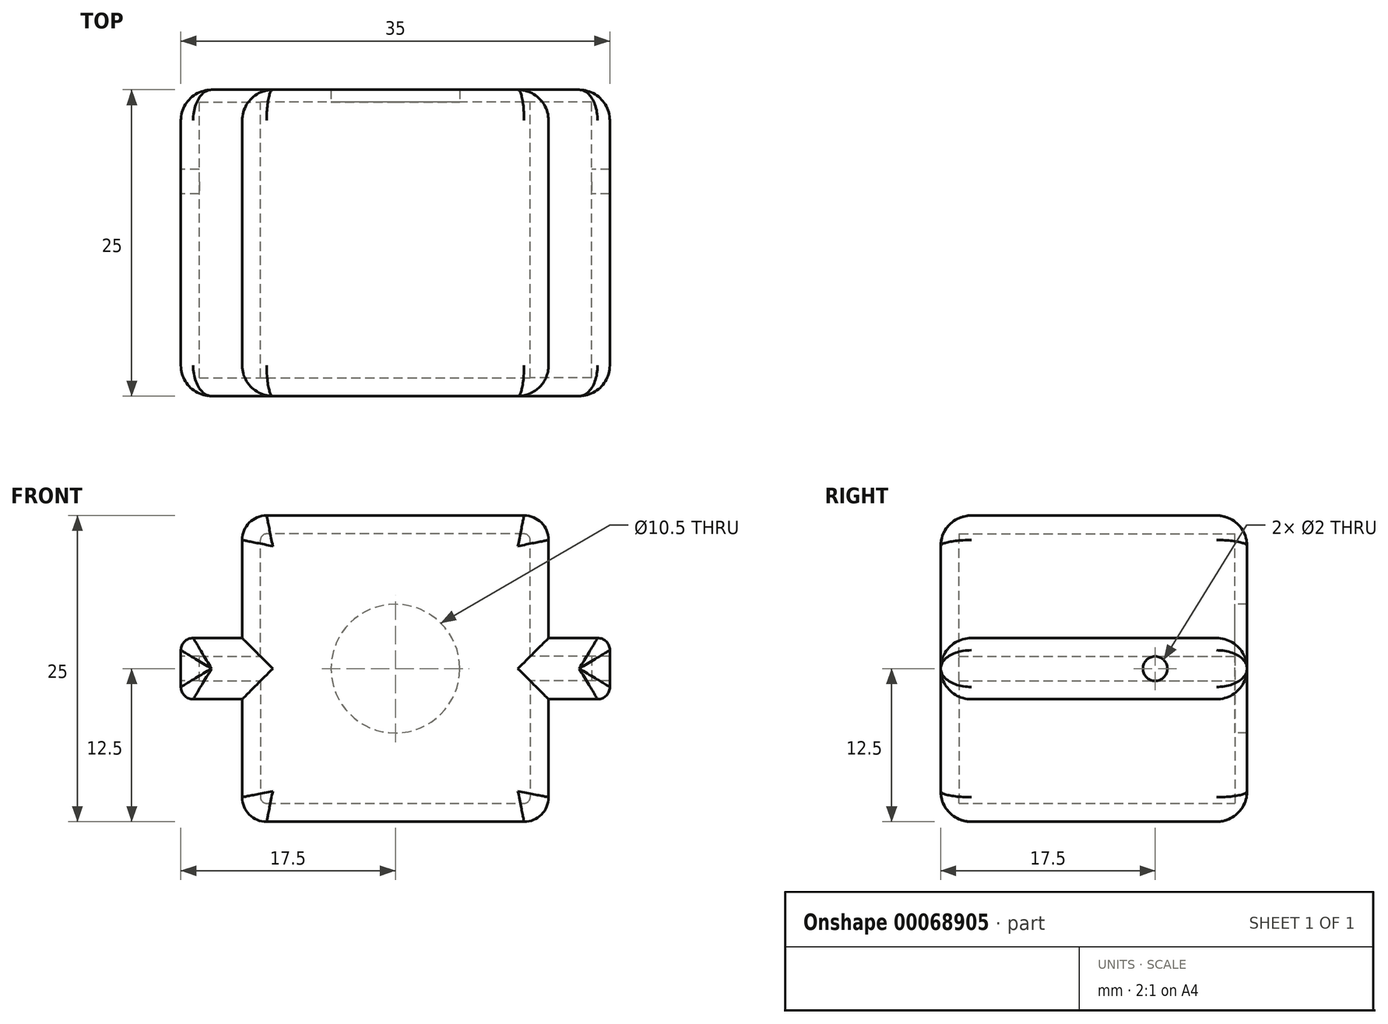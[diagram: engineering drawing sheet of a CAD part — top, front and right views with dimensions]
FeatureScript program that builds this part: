
annotation { "Feature Type Name" : "Feature", "Feature Type Description" : "" }
export const myFeature = defineFeature(function(context is Context, id is Id, definition is map)
    precondition{}
    {
        {
            var Q0;
            Q0=qCreatedBy(makeId("Front.planeOp"),FACE);
            var sketch = newSketch(context, id + "F0", { "sketchPlane" : qUnion([Q0])});
            skLineSegment(sketch, "E0", {"start": v(12.5, -2.5) * mm, "end": v(12.5, -10.5) * mm});
            skLineSegment(sketch, "E1", {"start": v(12.5, 2.5) * mm, "end": v(12.5, 10.5) * mm});
            skLineSegment(sketch, "E2", {"start": v(10.5, 12.5) * mm, "end": v(0, 12.5) * mm});
            skLineSegment(sketch, "E3", {"start": v(10.5, -12.5) * mm, "end": v(0, -12.5) * mm});
            skPoint(sketch, "E4.visualSharp", {"position": v(12.5, 12.5) * mm});
            skArc(sketch, "E4.filletArc", {"start": v(12.5, 10.5) * mm, "mid": v(11.91, 11.91) * mm, "end": v(10.5, 12.5) * mm});
            skPoint(sketch, "E5.visualSharp", {"position": v(12.5, -12.5) * mm});
            skArc(sketch, "E5.filletArc", {"start": v(10.5, -12.5) * mm, "mid": v(11.91, -11.91) * mm, "end": v(12.5, -10.5) * mm});
            skArc(sketch, "E6.MirrorCS", {"start": v(-12.5, 10.5) * mm, "mid": v(-11.91, 11.91) * mm, "end": v(-10.5, 12.5) * mm});
            skArc(sketch, "E7.MirrorCS", {"start": v(-10.5, -12.5) * mm, "mid": v(-11.91, -11.91) * mm, "end": v(-12.5, -10.5) * mm});
            skLineSegment(sketch, "E8.MirrorCS", {"start": v(-12.5, 2.5) * mm, "end": v(-12.5, 10.5) * mm});
            skLineSegment(sketch, "E9.MirrorCS", {"start": v(-10.5, 12.5) * mm, "end": v(0, 12.5) * mm});
            skLineSegment(sketch, "E10.MirrorCS", {"start": v(-12.5, -2.5) * mm, "end": v(-12.5, -10.5) * mm});
            skLineSegment(sketch, "E11.MirrorCS", {"start": v(-10.5, -12.5) * mm, "end": v(0, -12.5) * mm});
            skPoint(sketch, "E12.MirrorP", {"position": v(-12.5, -12.5) * mm});
            skPoint(sketch, "E13.MirrorP", {"position": v(-12.5, 12.5) * mm});
            skCircle(sketch, "E14", {"center": v(0, 0) * mm, "radius": 5.25 * mm});
            skLineSegment(sketch, "E15", {"start": v(17.5, 0) * mm, "end": v(17.5, 1.5) * mm});
            skLineSegment(sketch, "E16", {"start": v(16.5, 2.5) * mm, "end": v(12.5, 2.5) * mm});
            skPoint(sketch, "E17.visualSharp", {"position": v(17.5, 2.5) * mm});
            skArc(sketch, "E17.filletArc", {"start": v(17.5, 1.5) * mm, "mid": v(17.2, 2.2) * mm, "end": v(16.5, 2.5) * mm});
            skArc(sketch, "E18.MirrorCS", {"start": v(17.5, -1.5) * mm, "mid": v(17.2, -2.2) * mm, "end": v(16.5, -2.5) * mm});
            skLineSegment(sketch, "E19.MirrorCS", {"start": v(16.5, -2.5) * mm, "end": v(12.5, -2.5) * mm});
            skLineSegment(sketch, "E20.MirrorCS", {"start": v(17.5, 0) * mm, "end": v(17.5, -1.5) * mm});
            skPoint(sketch, "E21.MirrorP", {"position": v(17.5, -2.5) * mm});
            skArc(sketch, "E22.MirrorCS", {"start": v(-17.5, 1.5) * mm, "mid": v(-17.2, 2.2) * mm, "end": v(-16.5, 2.5) * mm});
            skLineSegment(sketch, "E23.MirrorCS", {"start": v(-17.5, 0) * mm, "end": v(-17.5, 1.5) * mm});
            skArc(sketch, "E24.MirrorCS", {"start": v(-17.5, -1.5) * mm, "mid": v(-17.2, -2.2) * mm, "end": v(-16.5, -2.5) * mm});
            skLineSegment(sketch, "E25.MirrorCS", {"start": v(-17.5, 0) * mm, "end": v(-17.5, -1.5) * mm});
            skPoint(sketch, "E26.MirrorP", {"position": v(-17.5, -2.5) * mm});
            skLineSegment(sketch, "E27.MirrorCS", {"start": v(-16.5, -2.5) * mm, "end": v(-12.5, -2.5) * mm});
            skLineSegment(sketch, "E28.MirrorCS", {"start": v(-16.5, 2.5) * mm, "end": v(-12.5, 2.5) * mm});
            skPoint(sketch, "E29.MirrorP", {"position": v(-17.5, 2.5) * mm});
            skPoint(sketch, "E30.orphan", {"position": v(-12.5, 0) * mm});
            skPoint(sketch, "E31.orphan", {"position": v(12.5, 0) * mm});
            skSolve(sketch);
        }
        {
            var Q0;
            Q0=qSketchRegion(id+"F0",true);
            extrude(context, id + "F1", {"entities" : qUnion([Q0]), "oppositeDirection" : true, "depth" : 1 * mm});
        }
        {
            var Q0;
            Q0=qCreatedBy(makeId("Front.planeOp"),FACE);
            var sketch = newSketch(context, id + "F2", { "sketchPlane" : qUnion([Q0])});
            skLineSegment(sketch, "E32", {"start": v(12.5, -2.5) * mm, "end": v(12.5, -10.5) * mm});
            skLineSegment(sketch, "E33", {"start": v(12.5, 2.5) * mm, "end": v(12.5, 10.5) * mm});
            skLineSegment(sketch, "E34", {"start": v(10.5, 12.5) * mm, "end": v(0, 12.5) * mm});
            skLineSegment(sketch, "E35", {"start": v(10.5, -12.5) * mm, "end": v(0, -12.5) * mm});
            skPoint(sketch, "E36.visualSharp", {"position": v(12.5, 12.5) * mm});
            skArc(sketch, "E36.filletArc", {"start": v(12.5, 10.5) * mm, "mid": v(11.91, 11.91) * mm, "end": v(10.5, 12.5) * mm});
            skPoint(sketch, "E37.visualSharp", {"position": v(12.5, -12.5) * mm});
            skArc(sketch, "E37.filletArc", {"start": v(10.5, -12.5) * mm, "mid": v(11.91, -11.91) * mm, "end": v(12.5, -10.5) * mm});
            skArc(sketch, "E38.MirrorCS", {"start": v(-12.5, 10.5) * mm, "mid": v(-11.91, 11.91) * mm, "end": v(-10.5, 12.5) * mm});
            skArc(sketch, "E39.MirrorCS", {"start": v(-10.5, -12.5) * mm, "mid": v(-11.91, -11.91) * mm, "end": v(-12.5, -10.5) * mm});
            skLineSegment(sketch, "E40.MirrorCS", {"start": v(-12.5, 2.5) * mm, "end": v(-12.5, 10.5) * mm});
            skLineSegment(sketch, "E41.MirrorCS", {"start": v(-10.5, 12.5) * mm, "end": v(0, 12.5) * mm});
            skLineSegment(sketch, "E42.MirrorCS", {"start": v(-12.5, -2.5) * mm, "end": v(-12.5, -10.5) * mm});
            skLineSegment(sketch, "E43.MirrorCS", {"start": v(-10.5, -12.5) * mm, "end": v(0, -12.5) * mm});
            skPoint(sketch, "E44.MirrorP", {"position": v(-12.87, -12.78) * mm});
            skPoint(sketch, "E45.MirrorP", {"position": v(-12.87, 12.22) * mm});
            skLineSegment(sketch, "E46", {"start": v(17.5, 0) * mm, "end": v(17.5, 1.5) * mm});
            skLineSegment(sketch, "E47", {"start": v(16.5, 2.5) * mm, "end": v(12.5, 2.5) * mm});
            skPoint(sketch, "E48.visualSharp", {"position": v(17.5, 2.5) * mm});
            skArc(sketch, "E48.filletArc", {"start": v(17.5, 1.5) * mm, "mid": v(17.2, 2.2) * mm, "end": v(16.5, 2.5) * mm});
            skArc(sketch, "E49.MirrorCS", {"start": v(17.5, -1.5) * mm, "mid": v(17.2, -2.2) * mm, "end": v(16.5, -2.5) * mm});
            skLineSegment(sketch, "E50.MirrorCS", {"start": v(16.5, -2.5) * mm, "end": v(12.5, -2.5) * mm});
            skLineSegment(sketch, "E51.MirrorCS", {"start": v(17.5, 0) * mm, "end": v(17.5, -1.5) * mm});
            skPoint(sketch, "E52.MirrorP", {"position": v(17.13, -2.78) * mm});
            skArc(sketch, "E53.MirrorCS", {"start": v(-17.5, 1.5) * mm, "mid": v(-17.2, 2.2) * mm, "end": v(-16.5, 2.5) * mm});
            skLineSegment(sketch, "E54.MirrorCS", {"start": v(-17.5, 0) * mm, "end": v(-17.5, 1.5) * mm});
            skArc(sketch, "E55.MirrorCS", {"start": v(-17.5, -1.5) * mm, "mid": v(-17.2, -2.2) * mm, "end": v(-16.5, -2.5) * mm});
            skLineSegment(sketch, "E56.MirrorCS", {"start": v(-17.5, 0) * mm, "end": v(-17.5, -1.5) * mm});
            skPoint(sketch, "E57.MirrorP", {"position": v(-17.87, -2.78) * mm});
            skLineSegment(sketch, "E58.MirrorCS", {"start": v(-16.5, -2.5) * mm, "end": v(-12.5, -2.5) * mm});
            skLineSegment(sketch, "E59.MirrorCS", {"start": v(-16.5, 2.5) * mm, "end": v(-12.5, 2.5) * mm});
            skPoint(sketch, "E60.MirrorP", {"position": v(-17.87, 2.22) * mm});
            skPoint(sketch, "E61.orphan", {"position": v(-12.5, 0) * mm});
            skPoint(sketch, "E62.orphan", {"position": v(12.5, 0) * mm});
            skSolve(sketch);
        }
        {
            var Q0;
            Q0=qSketchRegion(id+"F2",true);
            extrude(context, id + "F3", {"entities" : qUnion([Q0]), "depth" : 24 * mm});
        }
        {
            var Q0;
            Q0=makeQuery(id+"F3.opExtrude","CAP_FACE",FACE,{"disambiguationData":[OSD([sQuery(id+"F2.wireOp",EDGE,"E32"),sQuery(id+"F2.wireOp",EDGE,"E33"),sQuery(id+"F2.wireOp",EDGE,"E34"),sQuery(id+"F2.wireOp",EDGE,"E35"),sQuery(id+"F2.wireOp",EDGE,"E36.filletArc"),sQuery(id+"F2.wireOp",EDGE,"E37.filletArc"),sQuery(id+"F2.wireOp",EDGE,"E38.MirrorCS"),sQuery(id+"F2.wireOp",EDGE,"E39.MirrorCS"),sQuery(id+"F2.wireOp",EDGE,"E40.MirrorCS"),sQuery(id+"F2.wireOp",EDGE,"E41.MirrorCS"),sQuery(id+"F2.wireOp",EDGE,"E42.MirrorCS"),sQuery(id+"F2.wireOp",EDGE,"E43.MirrorCS"),sQuery(id+"F2.wireOp",EDGE,"E46"),sQuery(id+"F2.wireOp",EDGE,"E47"),sQuery(id+"F2.wireOp",EDGE,"E48.filletArc"),sQuery(id+"F2.wireOp",EDGE,"E49.MirrorCS"),sQuery(id+"F2.wireOp",EDGE,"E50.MirrorCS"),sQuery(id+"F2.wireOp",EDGE,"E51.MirrorCS"),sQuery(id+"F2.wireOp",EDGE,"E53.MirrorCS"),sQuery(id+"F2.wireOp",EDGE,"E54.MirrorCS"),sQuery(id+"F2.wireOp",EDGE,"E55.MirrorCS"),sQuery(id+"F2.wireOp",EDGE,"E56.MirrorCS"),sQuery(id+"F2.wireOp",EDGE,"E58.MirrorCS"),sQuery(id+"F2.wireOp",EDGE,"E59.MirrorCS")])],"isStart":true});
            shell(context, id + "F4", {"entities" : qUnion([Q0]), "thickness" : 1.5 * mm});
        }
        {
            var Q0;
            Q0=makeQuery(id+"F1.opExtrude","SWEPT_BODY",BODY,{"disambiguationData":[OSD([sQuery(id+"F0.wireOp",EDGE,"E0"),sQuery(id+"F0.wireOp",EDGE,"E1"),sQuery(id+"F0.wireOp",EDGE,"E2"),sQuery(id+"F0.wireOp",EDGE,"E3"),sQuery(id+"F0.wireOp",EDGE,"E4.filletArc"),sQuery(id+"F0.wireOp",EDGE,"E5.filletArc"),sQuery(id+"F0.wireOp",EDGE,"E6.MirrorCS"),sQuery(id+"F0.wireOp",EDGE,"E7.MirrorCS"),sQuery(id+"F0.wireOp",EDGE,"E8.MirrorCS"),sQuery(id+"F0.wireOp",EDGE,"E9.MirrorCS"),sQuery(id+"F0.wireOp",EDGE,"E10.MirrorCS"),sQuery(id+"F0.wireOp",EDGE,"E11.MirrorCS"),sQuery(id+"F0.wireOp",EDGE,"E14"),sQuery(id+"F0.wireOp",EDGE,"E15"),sQuery(id+"F0.wireOp",EDGE,"E16"),sQuery(id+"F0.wireOp",EDGE,"E17.filletArc"),sQuery(id+"F0.wireOp",EDGE,"E18.MirrorCS"),sQuery(id+"F0.wireOp",EDGE,"E19.MirrorCS"),sQuery(id+"F0.wireOp",EDGE,"E20.MirrorCS"),sQuery(id+"F0.wireOp",EDGE,"E22.MirrorCS"),sQuery(id+"F0.wireOp",EDGE,"E23.MirrorCS"),sQuery(id+"F0.wireOp",EDGE,"E24.MirrorCS"),sQuery(id+"F0.wireOp",EDGE,"E25.MirrorCS"),sQuery(id+"F0.wireOp",EDGE,"E27.MirrorCS"),sQuery(id+"F0.wireOp",EDGE,"E28.MirrorCS")])]});
            var Q1;
            Q1=makeQuery(id+"F3.opExtrude","SWEPT_BODY",BODY,{"disambiguationData":[OSD([sQuery(id+"F2.wireOp",EDGE,"E32"),sQuery(id+"F2.wireOp",EDGE,"E33"),sQuery(id+"F2.wireOp",EDGE,"E34"),sQuery(id+"F2.wireOp",EDGE,"E35"),sQuery(id+"F2.wireOp",EDGE,"E36.filletArc"),sQuery(id+"F2.wireOp",EDGE,"E37.filletArc"),sQuery(id+"F2.wireOp",EDGE,"E38.MirrorCS"),sQuery(id+"F2.wireOp",EDGE,"E39.MirrorCS"),sQuery(id+"F2.wireOp",EDGE,"E40.MirrorCS"),sQuery(id+"F2.wireOp",EDGE,"E41.MirrorCS"),sQuery(id+"F2.wireOp",EDGE,"E42.MirrorCS"),sQuery(id+"F2.wireOp",EDGE,"E43.MirrorCS"),sQuery(id+"F2.wireOp",EDGE,"E46"),sQuery(id+"F2.wireOp",EDGE,"E47"),sQuery(id+"F2.wireOp",EDGE,"E48.filletArc"),sQuery(id+"F2.wireOp",EDGE,"E49.MirrorCS"),sQuery(id+"F2.wireOp",EDGE,"E50.MirrorCS"),sQuery(id+"F2.wireOp",EDGE,"E51.MirrorCS"),sQuery(id+"F2.wireOp",EDGE,"E53.MirrorCS"),sQuery(id+"F2.wireOp",EDGE,"E54.MirrorCS"),sQuery(id+"F2.wireOp",EDGE,"E55.MirrorCS"),sQuery(id+"F2.wireOp",EDGE,"E56.MirrorCS"),sQuery(id+"F2.wireOp",EDGE,"E58.MirrorCS"),sQuery(id+"F2.wireOp",EDGE,"E59.MirrorCS")])]});
            booleanBodies(context, id + "F5", {"operationType" : BooleanOperationType.UNION, "tools" : qUnion([Q0, Q1])});
        }
        {
            var Q0;
            Q0=makeQuery(id+"F3.opExtrude","CAP_EDGE",EDGE,{"disambiguationData":[OSD([sQuery(id+"F2.wireOp",EDGE,"E34"),sQuery(id+"F2.wireOp",EDGE,"E41.MirrorCS")])],"isStart":false});
            var Q1;
            Q1=makeQuery(id+"F3.opExtrude","CAP_EDGE",EDGE,{"disambiguationData":[OSD([sQuery(id+"F2.wireOp",EDGE,"E35"),sQuery(id+"F2.wireOp",EDGE,"E43.MirrorCS")])],"isStart":false});
            var Q2;
            Q2=makeQuery(id+"F3.opExtrude","CAP_EDGE",EDGE,{"disambiguationData":[OSD([sQuery(id+"F2.wireOp",EDGE,"E59.MirrorCS")])],"isStart":false});
            var Q3;
            Q3=makeQuery(id+"F3.opExtrude","CAP_EDGE",EDGE,{"disambiguationData":[OSD([sQuery(id+"F2.wireOp",EDGE,"E47")])],"isStart":false});
            var Q4;
            Q4=makeQuery(id+"F1.opExtrude","CAP_EDGE",EDGE,{"disambiguationData":[OSD([sQuery(id+"F0.wireOp",EDGE,"E2"),sQuery(id+"F0.wireOp",EDGE,"E9.MirrorCS")])],"isStart":false});
            var Q5;
            Q5=makeQuery(id+"F1.opExtrude","CAP_EDGE",EDGE,{"disambiguationData":[OSD([sQuery(id+"F0.wireOp",EDGE,"E3"),sQuery(id+"F0.wireOp",EDGE,"E11.MirrorCS")])],"isStart":false});
            var Q6;
            Q6=makeQuery(id+"F1.opExtrude","CAP_EDGE",EDGE,{"disambiguationData":[OSD([sQuery(id+"F0.wireOp",EDGE,"E19.MirrorCS")])],"isStart":false});
            var Q7;
            Q7=makeQuery(id+"F1.opExtrude","CAP_EDGE",EDGE,{"disambiguationData":[OSD([sQuery(id+"F0.wireOp",EDGE,"E27.MirrorCS")])],"isStart":false});
            fillet(context, id + "F6", {"entities" : qUnion([Q0, Q1, Q2, Q3, Q4, Q5, Q6, Q7]), "radius" : 2.5 * mm, "tangentPropagation" : true, "allowEdgeOverflow" : false});
        }
        {
            var Q0;
            Q0=makeQuery(id+"F5.opBoolean","MERGE",FACE,{"derivedFrom":[makeQuery(id+"F1.opExtrude","SWEPT_FACE",FACE,{"disambiguationData":[OSD([sQuery(id+"F0.wireOp",EDGE,"E23.MirrorCS"),sQuery(id+"F0.wireOp",EDGE,"E25.MirrorCS")])]}),makeQuery(id+"F3.opExtrude","SWEPT_FACE",FACE,{"disambiguationData":[OSD([sQuery(id+"F2.wireOp",EDGE,"E54.MirrorCS"),sQuery(id+"F2.wireOp",EDGE,"E56.MirrorCS")])]})]});
            var sketch = newSketch(context, id + "F7", { "sketchPlane" : qUnion([Q0])});
            skCircle(sketch, "E63", {"center": v(6.5, 0) * mm, "radius": 1 * mm});
            skLineSegment(sketch, "E64", {"start": v(24, 0) * mm, "end": v(28.76, 0) * mm});
            skSolve(sketch);
        }
        {
            var Q0;
            Q0=sQuery(id+"F7.wireOp",VERTEX,"E63.center");
            var Q1;
            Q1=makeQuery(id+"F1.opExtrude","SWEPT_BODY",BODY,{"disambiguationData":[OSD([sQuery(id+"F0.wireOp",EDGE,"E0"),sQuery(id+"F0.wireOp",EDGE,"E1"),sQuery(id+"F0.wireOp",EDGE,"E2"),sQuery(id+"F0.wireOp",EDGE,"E3"),sQuery(id+"F0.wireOp",EDGE,"E4.filletArc"),sQuery(id+"F0.wireOp",EDGE,"E5.filletArc"),sQuery(id+"F0.wireOp",EDGE,"E6.MirrorCS"),sQuery(id+"F0.wireOp",EDGE,"E7.MirrorCS"),sQuery(id+"F0.wireOp",EDGE,"E8.MirrorCS"),sQuery(id+"F0.wireOp",EDGE,"E9.MirrorCS"),sQuery(id+"F0.wireOp",EDGE,"E10.MirrorCS"),sQuery(id+"F0.wireOp",EDGE,"E11.MirrorCS"),sQuery(id+"F0.wireOp",EDGE,"E14"),sQuery(id+"F0.wireOp",EDGE,"E15"),sQuery(id+"F0.wireOp",EDGE,"E16"),sQuery(id+"F0.wireOp",EDGE,"E17.filletArc"),sQuery(id+"F0.wireOp",EDGE,"E18.MirrorCS"),sQuery(id+"F0.wireOp",EDGE,"E19.MirrorCS"),sQuery(id+"F0.wireOp",EDGE,"E20.MirrorCS"),sQuery(id+"F0.wireOp",EDGE,"E22.MirrorCS"),sQuery(id+"F0.wireOp",EDGE,"E23.MirrorCS"),sQuery(id+"F0.wireOp",EDGE,"E24.MirrorCS"),sQuery(id+"F0.wireOp",EDGE,"E25.MirrorCS"),sQuery(id+"F0.wireOp",EDGE,"E27.MirrorCS"),sQuery(id+"F0.wireOp",EDGE,"E28.MirrorCS")])]});
            hole(context, id + "F8", {"style" : HoleStyle.SIMPLE, "holeDiameter" : 2 * mm, "endStyle" : HoleEndStyle.THROUGH, "locations" : qUnion([Q0]), "scope" : qUnion([Q1])});
        }
    });
